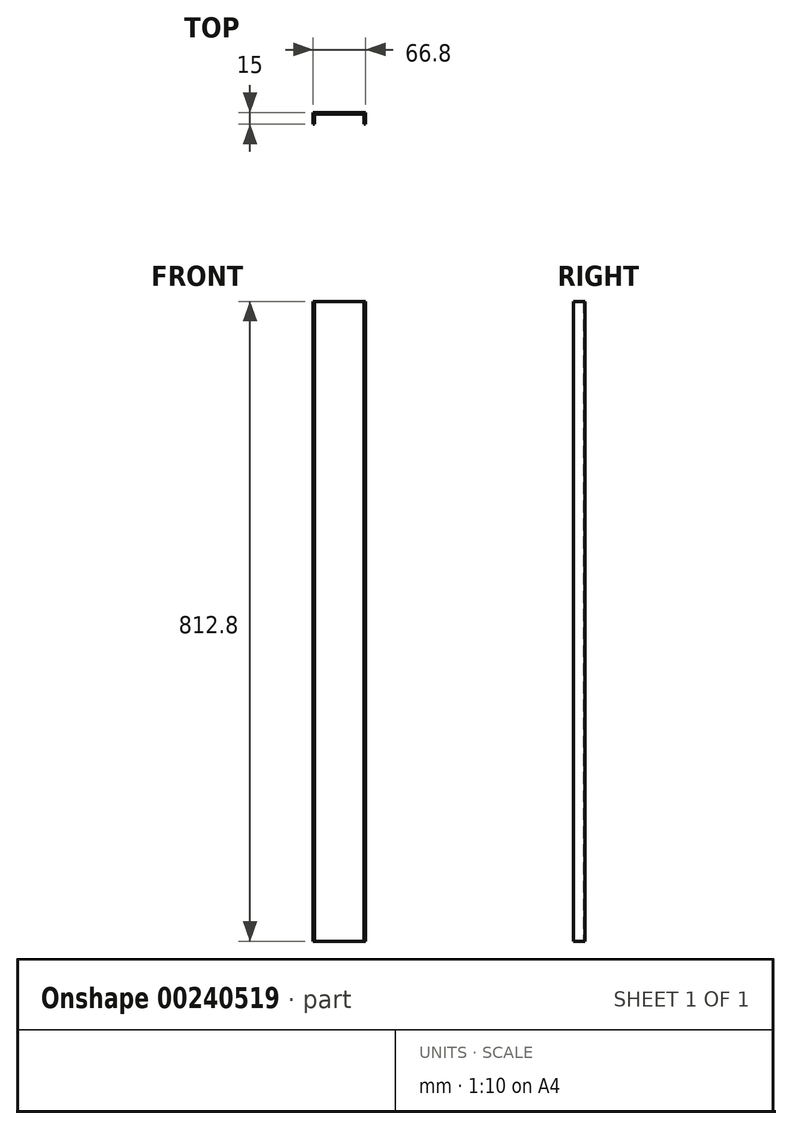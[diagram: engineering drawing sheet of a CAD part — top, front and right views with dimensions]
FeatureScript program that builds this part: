
annotation { "Feature Type Name" : "Feature", "Feature Type Description" : "" }
export const myFeature = defineFeature(function(context is Context, id is Id, definition is map)
    precondition{}
    {
        {
            var Q0;
            Q0=qCreatedBy(makeId("Top.planeOp"),FACE);
            var sketch = newSketch(context, id + "F0", { "sketchPlane" : qUnion([Q0])});
            skLineSegment(sketch, "E0", {"start": v(-33.18, -15.17) * mm, "end": v(-33.18, -0.17) * mm});
            skLineSegment(sketch, "E1", {"start": v(-33.18, -0.17) * mm, "end": v(33.62, -0.17) * mm});
            skLineSegment(sketch, "E2", {"start": v(33.62, -0.17) * mm, "end": v(33.62, -15.17) * mm});
            skLineSegment(sketch, "E3", {"start": v(33.62, -15.17) * mm, "end": v(31.62, -15.17) * mm});
            skLineSegment(sketch, "E4", {"start": v(31.62, -15.17) * mm, "end": v(31.62, -2.17) * mm});
            skLineSegment(sketch, "E5", {"start": v(31.62, -2.17) * mm, "end": v(-31.18, -2.17) * mm});
            skLineSegment(sketch, "E6", {"start": v(-31.18, -2.17) * mm, "end": v(-31.18, -15.17) * mm});
            skLineSegment(sketch, "E7", {"start": v(-31.18, -15.17) * mm, "end": v(-33.18, -15.17) * mm});
            skSolve(sketch);
        }
        {
            var Q0;
            Q0 = qSketchRegion(id + "F0", true);
            extrude(context, id + "F1", {"entities" : qUnion([Q0]), "depth" : 812.8 * mm});
        }
    });
